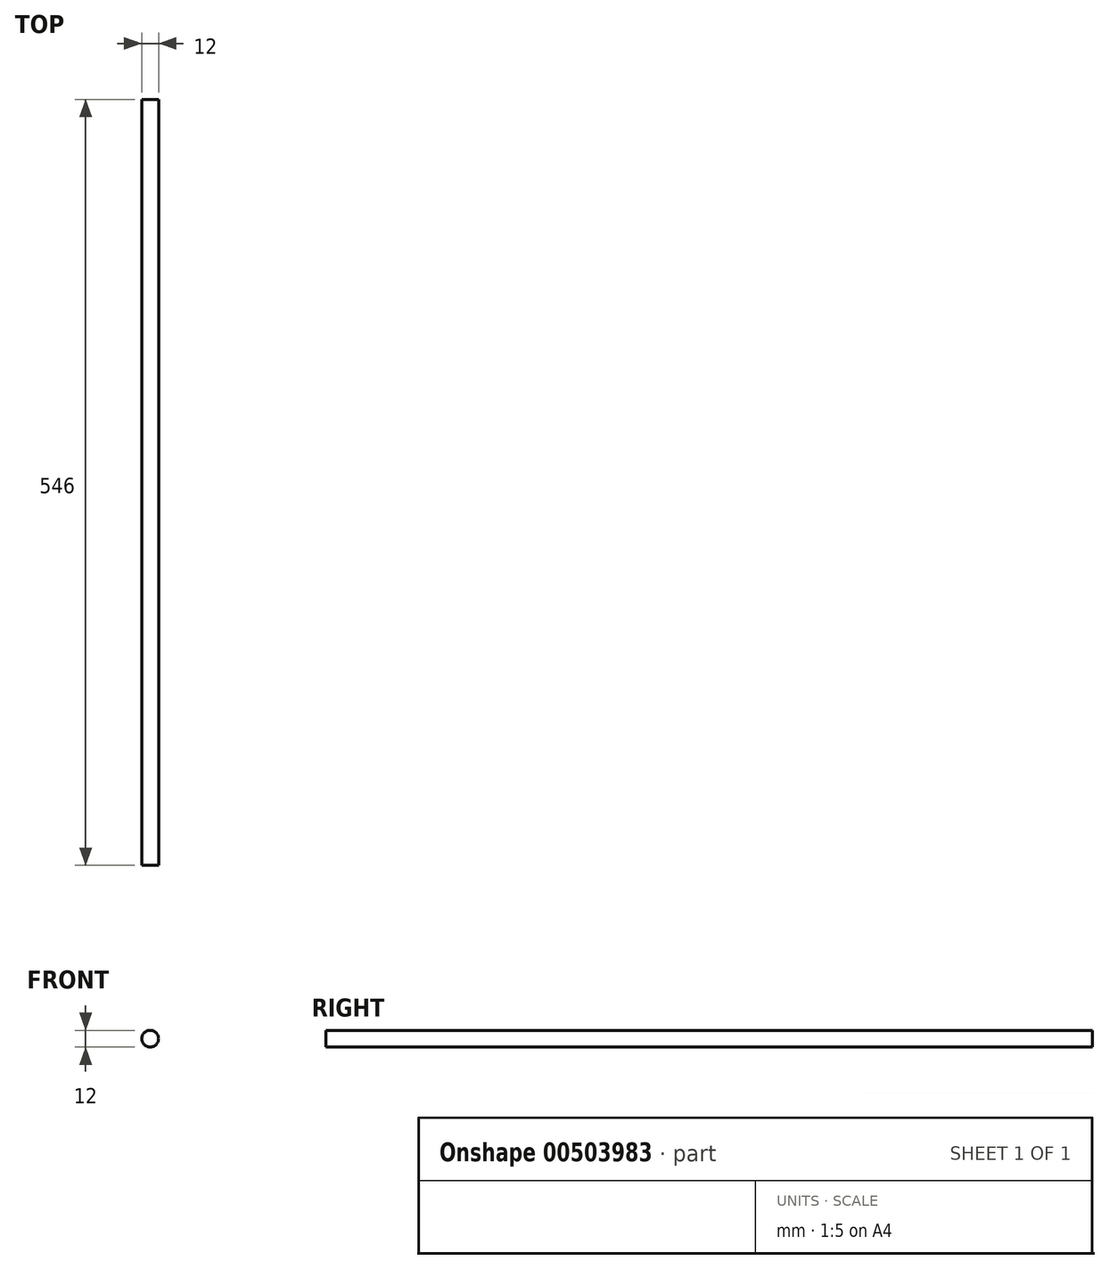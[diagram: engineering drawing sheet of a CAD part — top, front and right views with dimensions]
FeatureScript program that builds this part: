
annotation { "Feature Type Name" : "Feature", "Feature Type Description" : "" }
export const myFeature = defineFeature(function(context is Context, id is Id, definition is map)
    precondition{}
    {
        {
            var Q0;
            Q0=qCreatedBy(makeId("Front.planeOp"),FACE);
            var sketch = newSketch(context, id + "F0", { "sketchPlane" : qUnion([Q0])});
            skCircle(sketch, "E0", {"center": v(0, 0) * mm, "radius": 6 * mm});
            skSolve(sketch);
        }
        {
            var Q0;
            Q0=makeQuery(id+"F0.imprint","IMPRINT",FACE,{"disambiguationData":[TD([[makeQuery(id+"F0.imprint","IMPRINT",EDGE,{"derivedFrom":sQuery(id+"F0.wireOp",EDGE,"E0")}),1.0]])]});
            extrude(context, id + "F1", {"entities" : qUnion([Q0]), "depth" : 546 * mm, "offsetDistance" : 25 * mm});
        }
    });
